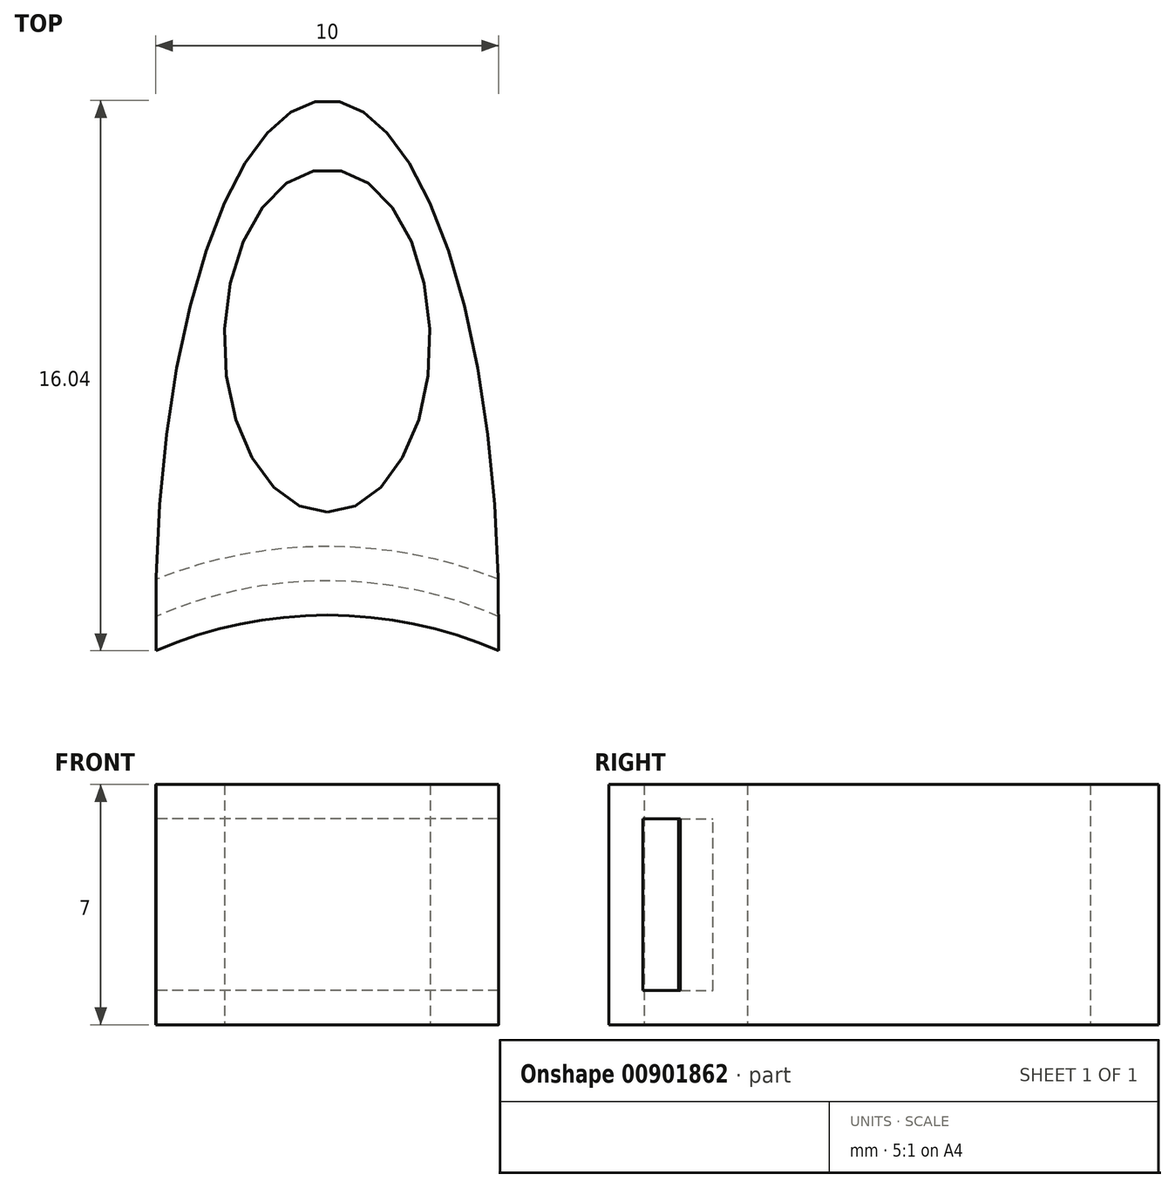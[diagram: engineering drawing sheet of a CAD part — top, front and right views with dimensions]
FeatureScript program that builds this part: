
annotation { "Feature Type Name" : "Feature", "Feature Type Description" : "" }
export const myFeature = defineFeature(function(context is Context, id is Id, definition is map)
    precondition{}
    {
        {
            var Q0;
            Q0=qCreatedBy(makeId("Top.planeOp"),FACE);
            var sketch = newSketch(context, id + "F0", { "sketchPlane" : qUnion([Q0])});
            skEllipticalArc(sketch, "E0", {});
            skArc(sketch, "E1", {"start": v(4.99, -1.04) * mm, "mid": v(0, 0) * mm, "end": v(-4.99, -1.04) * mm});
            skPoint(sketch, "E1.centerSnap0", {"position": v(0, -15) * mm});
            skEllipse(sketch, "E2", {"center": v(0, 8) * mm, "majorRadius": 5 * mm, "minorRadius": 3 * mm, "majorAxis": v(0, -1)});
            skPoint(sketch, "E3.end.orphan", {"position": v(-6, -1.53) * mm});
            skPoint(sketch, "E4.orphan", {"position": v(6, -1.53) * mm});
            skLineSegment(sketch, "E5.top", {"start": v(-5.98, 0.46) * mm, "end": v(-5.99, 0.46) * mm});
            skLineSegment(sketch, "E6.bottom", {"start": v(4.99, -1.04) * mm, "end": v(5.99, -1.04) * mm});
            skLineSegment(sketch, "E6.top", {"start": v(5.98, 0.46) * mm, "end": v(5.99, 0.46) * mm});
            skPoint(sketch, "E7.newPointA", {"position": v(-4.99, 0.46) * mm});
            skPoint(sketch, "E8.newPointB", {"position": v(4.99, 0.46) * mm});
            skEllipticalArc(sketch, "E9", {});
            skEllipticalArc(sketch, "E10.trimOffspring", {});
            const initialGuessF0  = {"E0": [0, 0, 0, -1, 0.015, 0.005, 1.6662588950214412, 4.616926412158144], "E9": [0, 0, 0, 1, 0.015, 0.005, 4.643111327906802, 4.807851548611234], "E10.trimOffspring": [0, 0, 0, 1, 0.015, 0.005, 1.4753337585683504, 1.6400739792727843]};
            skSetInitialGuess(sketch, initialGuessF0);
            skSolve(sketch);
        }
        {
            var Q0;
            Q0 = qSketchRegion(id + "F0", true);
            extrude(context, id + "F1", {"entities" : qUnion([Q0]), "depth" : 7 * mm, "offsetDistance" : 25 * mm});
        }
        {
            var Q0;
            Q0=makeQuery(id+"F1.opExtrude","CAP_FACE",FACE,{"disambiguationData":[OSD([sQuery(id+"F0.wireOp",EDGE,"E0"),sQuery(id+"F0.wireOp",EDGE,"E1"),sQuery(id+"F0.wireOp",EDGE,"E2"),sQuery(id+"F0.wireOp",EDGE,"E9"),sQuery(id+"F0.wireOp",EDGE,"E10.trimOffspring")])],"isStart":false});
            cPlane(context, id + "F2", {"entities" : qUnion([Q0]), "cplaneType" : CPlaneType.OFFSET, "offset" : 1 * mm, "oppositeDirection" : true, "width" : 150 * mm, "height" : 150 * mm});
        }
        {
            var Q0;
            Q0=qCreatedBy(id+"F2.planeOp",FACE);
            var sketch = newSketch(context, id + "F3", { "sketchPlane" : qUnion([Q0])});
            skArc(sketch, "E11", {"start": v(5, -0.04) * mm, "mid": v(0, 1) * mm, "end": v(-5, -0.04) * mm});
            skArc(sketch, "E12", {"start": v(4.99, 1.04) * mm, "mid": v(0, 2) * mm, "end": v(-4.99, 1.04) * mm});
            skEllipticalArc(sketch, "E13.0", {});
            skEllipticalArc(sketch, "E14.trimOffspring", {});
            skPoint(sketch, "E15.orphan", {"position": v(-4.99, -1.04) * mm});
            skPoint(sketch, "E16.orphan", {"position": v(4.99, -1.04) * mm});
            const initialGuessF3  = {"E13.0": [0, 0, 0, 1, 0.015, 0.005, 4.7094855386530785, 4.782096829926598], "E14.trimOffspring": [0, 0, 0, 1, 0.015, 0.005, 1.5010884772529876, 1.573699768526508]};
            skSetInitialGuess(sketch, initialGuessF3);
            skSolve(sketch);
        }
        {
            var Q0;
            Q0 = qSketchRegion(id + "F3", true);
            extrude(context, id + "F4", {"entities" : qUnion([Q0]), "operationType" : NewBodyOperationType.REMOVE, "oppositeDirection" : true, "depth" : 5 * mm, "offsetDistance" : 25 * mm});
        }
    });
